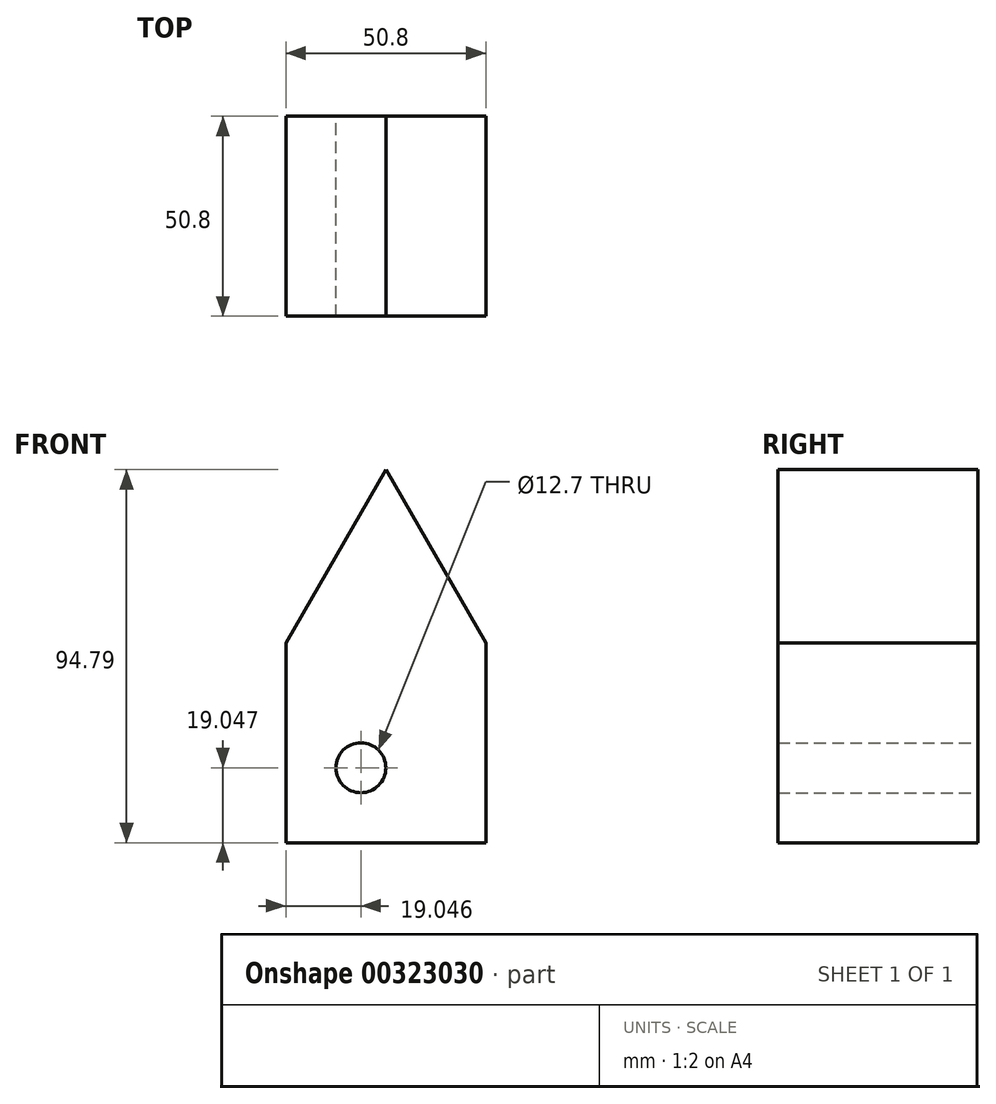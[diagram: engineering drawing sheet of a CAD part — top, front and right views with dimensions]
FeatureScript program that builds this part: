
annotation { "Feature Type Name" : "Feature", "Feature Type Description" : "" }
export const myFeature = defineFeature(function(context is Context, id is Id, definition is map)
    precondition{}
    {
        {
            var Q0;
            Q0=qCreatedBy(makeId("Front.planeOp"),FACE);
            var sketch = newSketch(context, id + "F0", { "sketchPlane" : qUnion([Q0])});
            skLineSegment(sketch, "E0.top", {"start": v(-6.62, -49.1) * mm, "end": v(44.18, -49.1) * mm});
            skLineSegment(sketch, "E0.left", {"start": v(-6.62, 1.7) * mm, "end": v(-6.62, -49.1) * mm});
            skLineSegment(sketch, "E0.right", {"start": v(44.18, 1.7) * mm, "end": v(44.18, -49.1) * mm});
            skLineSegment(sketch, "E1", {"start": v(18.78, 45.7) * mm, "end": v(44.18, 1.7) * mm});
            skPoint(sketch, "E1.startSnap0", {"position": v(18.78, 1.7) * mm});
            skLineSegment(sketch, "E2", {"start": v(18.78, 45.7) * mm, "end": v(-6.62, 1.7) * mm});
            skCircle(sketch, "E3", {"center": v(12.43, -30.04) * mm, "radius": 6.35 * mm});
            skSolve(sketch);
        }
        {
            var Q0;
            Q0=makeQuery(id+"F0.imprint","IMPRINT",FACE,{"disambiguationData":[TD([[makeQuery(id+"F0.imprint","IMPRINT",EDGE,{"derivedFrom":sQuery(id+"F0.wireOp",EDGE,"E0.top")}),1.0]])]});
            extrude(context, id + "F1", {"entities" : qUnion([Q0]), "depth" : 50.8 * mm});
        }
    });
